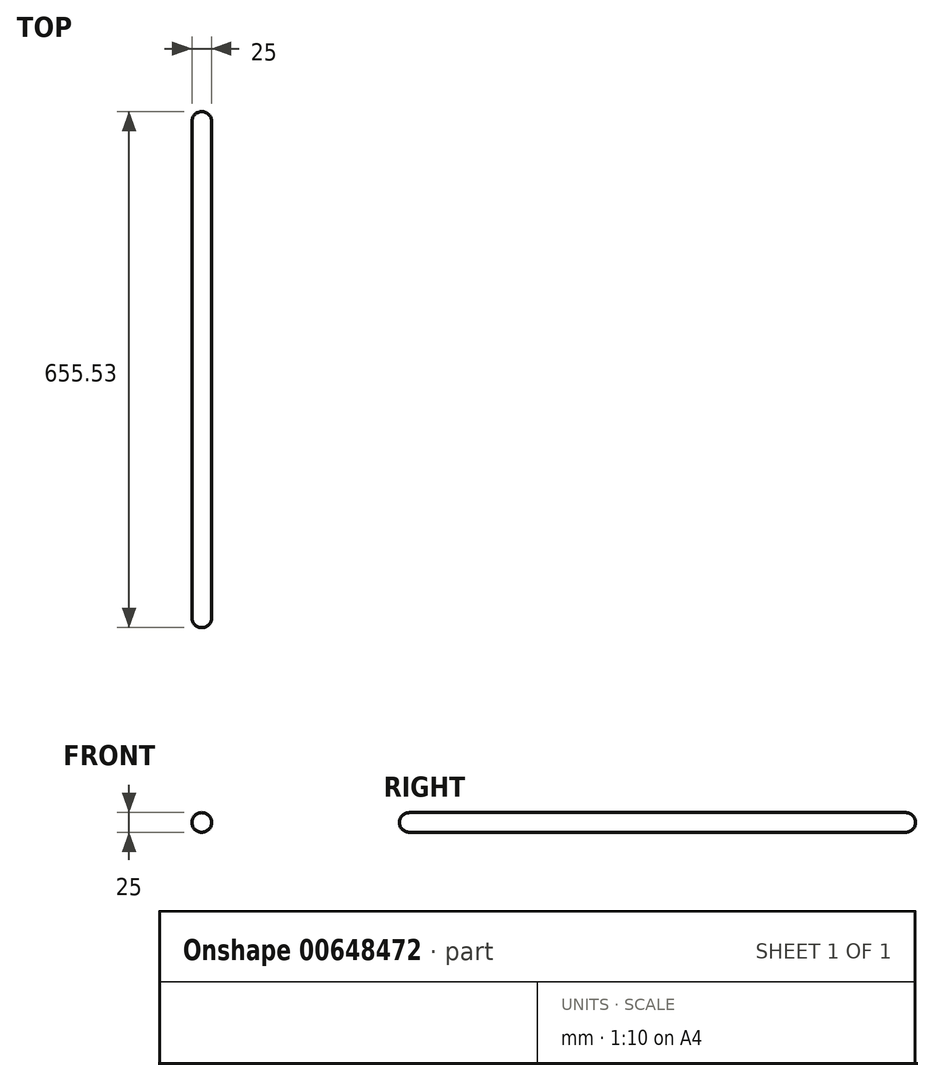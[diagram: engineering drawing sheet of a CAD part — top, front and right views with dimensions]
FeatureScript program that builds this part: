
annotation { "Feature Type Name" : "Feature", "Feature Type Description" : "" }
export const myFeature = defineFeature(function(context is Context, id is Id, definition is map)
    precondition{}
    {
        {
            var Q0;
            Q0=qCreatedBy(makeId("Top.planeOp"),FACE);
            var sketch = newSketch(context, id + "F0", { "sketchPlane" : qUnion([Q0])});
            skLineSegment(sketch, "E0", {"start": v(0, 0) * mm, "end": v(0, -55.53) * mm});
            skSolve(sketch);
        }
        {
            var Q0;
            Q0=qCreatedBy(makeId("Right.planeOp"),FACE);
            var sketch = newSketch(context, id + "F1", { "sketchPlane" : qUnion([Q0])});
            skLineSegment(sketch, "E1", {"start": v(-75.02, 61.15) * mm, "end": v(-75.02, 20.6) * mm});
            skArc(sketch, "E2", {"start": v(-75.02, 20.6) * mm, "mid": v(-69.62, 6.67) * mm, "end": v(-56.24, 0) * mm});
            skSolve(sketch);
        }
        {
            var Q0;
            Q0=sQuery(id+"F1.wireOp",EDGE,"E2");
            var Q1;
            Q1=sQuery(id+"F0.wireOp",EDGE,"E0");
            var Q2;
            Q2=sQuery(id+"F1.wireOp",EDGE,"E1");
            extrude(context, id + "F2", {"bodyType" : ToolBodyType.SURFACE, "surfaceEntities" : qUnion([Q0, Q1, Q2]), "depth" : 25 * mm, "offsetDistance" : 25 * mm});
        }
        {
            var Q0;
            Q0=makeQuery(id+"F2.opExtrude","SWEPT_FACE",FACE,{"disambiguationData":[OSD([sQuery(id+"F0.wireOp",EDGE,"E0")])]});
            var sketch = newSketch(context, id + "F3", { "sketchPlane" : qUnion([Q0])});
            skSolve(sketch);
        }
        {
            var Q0;
            Q0=makeQuery(id+"F3.imprint","IMPRINT",FACE,{"disambiguationData":[TD([[makeQuery(id+"F3.imprint","IMPRINT",EDGE,{"derivedFrom":makeQuery(id+"F2.opExtrude","SWEPT_EDGE",EDGE,{"disambiguationData":[OSD([sQuery(id+"F0.wireOp",VERTEX,"E0.start")])]})}),-1.0]])]});
            extrude(context, id + "F4", {"entities" : qUnion([Q0]), "depth" : 25 * mm, "offsetDistance" : 25 * mm});
        }
        {
            var Q0;
            Q0=makeQuery(id+"F4.opExtrude","SWEPT_FACE",FACE,{"disambiguationData":[OSD([sQuery(id+"F0.wireOp",VERTEX,"E0.start")])]});
            extrude(context, id + "F5", {"entities" : qUnion([Q0]), "operationType" : NewBodyOperationType.ADD, "depth" : 600 * mm, "offsetDistance" : 25 * mm});
        }
        {
            var Q0;
            {var subQ0=sQuery(id+"F0.wireOp",VERTEX,"E0.start");Q0=makeQuery(id+"F5.boolean.opBoolean","MERGE",FACE,{"derivedFrom":[makeQuery(id+"F4.opExtrude","CAP_FACE",FACE,{"disambiguationData":[OSD([subQ0,sQuery(id+"F0.wireOp",VERTEX,"E0.end"),sQuery(id+"F0.wireOp",EDGE,"E0")])],"isStart":false}),makeQuery(id+"F5.opExtrude","SWEPT_FACE",FACE,{"disambiguationData":[OSD([subQ0]),TDD([makeQuery(id+"F4.opExtrude","CAP_EDGE",EDGE,{"disambiguationData":[OSD([subQ0])],"isStart":false})])]})]});}
            var Q1;
            {var subQ0=sQuery(id+"F0.wireOp",EDGE,"E0");var subQ1=makeQuery(id+"F2.opExtrude","CAP_EDGE",EDGE,{"disambiguationData":[OSD([subQ0])],"isStart":false});var subQ2=sQuery(id+"F0.wireOp",VERTEX,"E0.start");Q1=makeQuery(id+"F5.boolean.opBoolean","MERGE",FACE,{"derivedFrom":[makeQuery(id+"F4.opExtrude","SWEPT_FACE",FACE,{"disambiguationData":[OSD([subQ0]),TDD([makeQuery(id+"F3.imprint","IMPRINT",EDGE,{"derivedFrom":subQ1})])]}),makeQuery(id+"F5.opExtrude","SWEPT_FACE",FACE,{"disambiguationData":[OSD([subQ2,subQ0]),TDD([makeQuery(id+"F4.opExtrude","SWEPT_EDGE",EDGE,{"disambiguationData":[OSD([subQ2,subQ0]),TDD([makeQuery(id+"F3.imprint","INTERSECT",VERTEX,{"derivedFrom":[makeQuery(id+"F2.opExtrude","SWEPT_EDGE",EDGE,{"disambiguationData":[OSD([subQ2])]}),subQ1]})])]})])]})]});}
            fillet(context, id + "F6", {"entities" : qUnion([Q0, Q1]), "radius" : 12.5 * mm, "tangentPropagation" : true, "allowEdgeOverflow" : false});
        }
        {
            var Q0;
            {var subQ0=sQuery(id+"F0.wireOp",EDGE,"E0");var subQ1=makeQuery(id+"F2.opExtrude","CAP_EDGE",EDGE,{"disambiguationData":[OSD([subQ0])],"isStart":true});var subQ2=sQuery(id+"F0.wireOp",VERTEX,"E0.start");Q0=makeQuery(id+"F5.boolean.opBoolean","MERGE",FACE,{"derivedFrom":[makeQuery(id+"F4.opExtrude","SWEPT_FACE",FACE,{"disambiguationData":[OSD([subQ0]),TDD([makeQuery(id+"F3.imprint","IMPRINT",EDGE,{"derivedFrom":subQ1})])]}),makeQuery(id+"F5.opExtrude","SWEPT_FACE",FACE,{"disambiguationData":[OSD([subQ2,subQ0]),TDD([makeQuery(id+"F4.opExtrude","SWEPT_EDGE",EDGE,{"disambiguationData":[OSD([subQ2,subQ0]),TDD([makeQuery(id+"F3.imprint","INTERSECT",VERTEX,{"derivedFrom":[makeQuery(id+"F2.opExtrude","SWEPT_EDGE",EDGE,{"disambiguationData":[OSD([subQ2])]}),subQ1]})])]})])]})]});}
            var Q1;
            {var subQ0=sQuery(id+"F0.wireOp",VERTEX,"E0.start");Q1=makeQuery(id+"F5.boolean.opBoolean","MERGE",FACE,{"derivedFrom":[makeQuery(id+"F4.opExtrude","CAP_FACE",FACE,{"disambiguationData":[OSD([subQ0,sQuery(id+"F0.wireOp",VERTEX,"E0.end"),sQuery(id+"F0.wireOp",EDGE,"E0")])],"isStart":true}),makeQuery(id+"F5.opExtrude","SWEPT_FACE",FACE,{"disambiguationData":[OSD([subQ0]),TDD([makeQuery(id+"F4.opExtrude","CAP_EDGE",EDGE,{"disambiguationData":[OSD([subQ0])],"isStart":true})])]})]});}
            fillet(context, id + "F7", {"entities" : qUnion([Q0, Q1]), "radius" : 12.5 * mm, "tangentPropagation" : true, "allowEdgeOverflow" : false});
        }
    });
